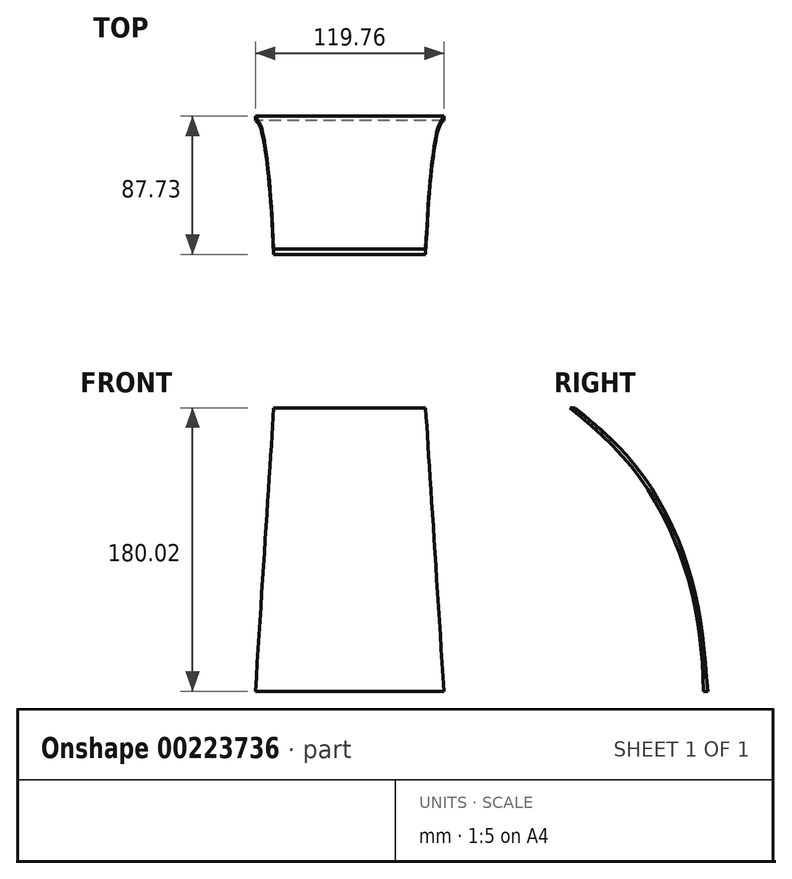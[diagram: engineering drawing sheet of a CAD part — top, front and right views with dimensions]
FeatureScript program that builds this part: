
annotation { "Feature Type Name" : "Feature", "Feature Type Description" : "" }
export const myFeature = defineFeature(function(context is Context, id is Id, definition is map)
    precondition{}
    {
        {
            var Q0;
            Q0=qCreatedBy(makeId("Right.planeOp"),FACE);
            var sketch = newSketch(context, id + "F0", { "sketchPlane" : qUnion([Q0])});
            skFitSpline(sketch, "E0", {"points": [v(0, 0) * mm, v(-8.56, 66.9) * mm, v(-41.4, 136.72) * mm, v(-84.92, 180) * mm], "startDerivative": vector(-7.48, 202.33) * mm, "endDerivative": vector(-149.25, 121.4) * mm});
            skFitSpline(sketch, "E1", {"points": [v(2.8, 0) * mm, v(-6.56, 67.34) * mm, v(-38.96, 137.63) * mm, v(-81.69, 180.02) * mm], "startDerivative": vector(-20.83, 203.27) * mm, "endDerivative": vector(-149.25, 121.4) * mm});
            skLineSegment(sketch, "E2", {"start": v(-84.92, 180) * mm, "end": v(-81.69, 180.02) * mm});
            skLineSegment(sketch, "E3", {"start": v(0, 0) * mm, "end": v(2.8, 0) * mm});
            skSolve(sketch);
        }
        {
            var Q0;
            Q0=qSketchRegion(id+"F0",true);
            extrude(context, id + "F1", {"entities" : qUnion([Q0]), "depth" : 120 * mm});
        }
        {
            var Q0;
            Q0=qCreatedBy(makeId("Front.planeOp"),FACE);
            cPlane(context, id + "F2", {"entities" : qUnion([Q0]), "cplaneType" : CPlaneType.OFFSET, "offset" : 10 * mm, "oppositeDirection" : true, "width" : 150 * mm, "height" : 150 * mm});
        }
        {
            var Q0;
            Q0=qCreatedBy(id+"F2.planeOp",FACE);
            var sketch = newSketch(context, id + "F3", { "sketchPlane" : qUnion([Q0])});
            skLineSegment(sketch, "E4", {"start": v(120.5, -9.47) * mm, "end": v(105.86, 216.24) * mm});
            skLineSegment(sketch, "E5", {"start": v(105.86, 216.24) * mm, "end": v(140, 216.24) * mm});
            skLineSegment(sketch, "E6", {"start": v(140, 216.24) * mm, "end": v(140, -5.65) * mm});
            skLineSegment(sketch, "E7", {"start": v(140, -5.65) * mm, "end": v(120.5, -9.47) * mm});
            skLineSegment(sketch, "E8", {"start": v(60, 166.82) * mm, "end": v(60, -16.45) * mm, "construction": true});
            skLineSegment(sketch, "E9.MirrorCS", {"start": v(-0.5, -9.47) * mm, "end": v(14.14, 216.24) * mm});
            skLineSegment(sketch, "E10.MirrorCS", {"start": v(14.14, 216.24) * mm, "end": v(-20, 216.24) * mm});
            skLineSegment(sketch, "E11.MirrorCS", {"start": v(-20, -5.65) * mm, "end": v(-0.5, -9.47) * mm});
            skLineSegment(sketch, "E12.MirrorCS", {"start": v(-20, 216.24) * mm, "end": v(-20, -5.65) * mm});
            skSolve(sketch);
        }
        {
            var Q0;
            Q0=qSketchRegion(id+"F3",true);
            extrude(context, id + "F4", {"entities" : qUnion([Q0]), "operationType" : NewBodyOperationType.REMOVE, "depth" : 150 * mm});
        }
    });
